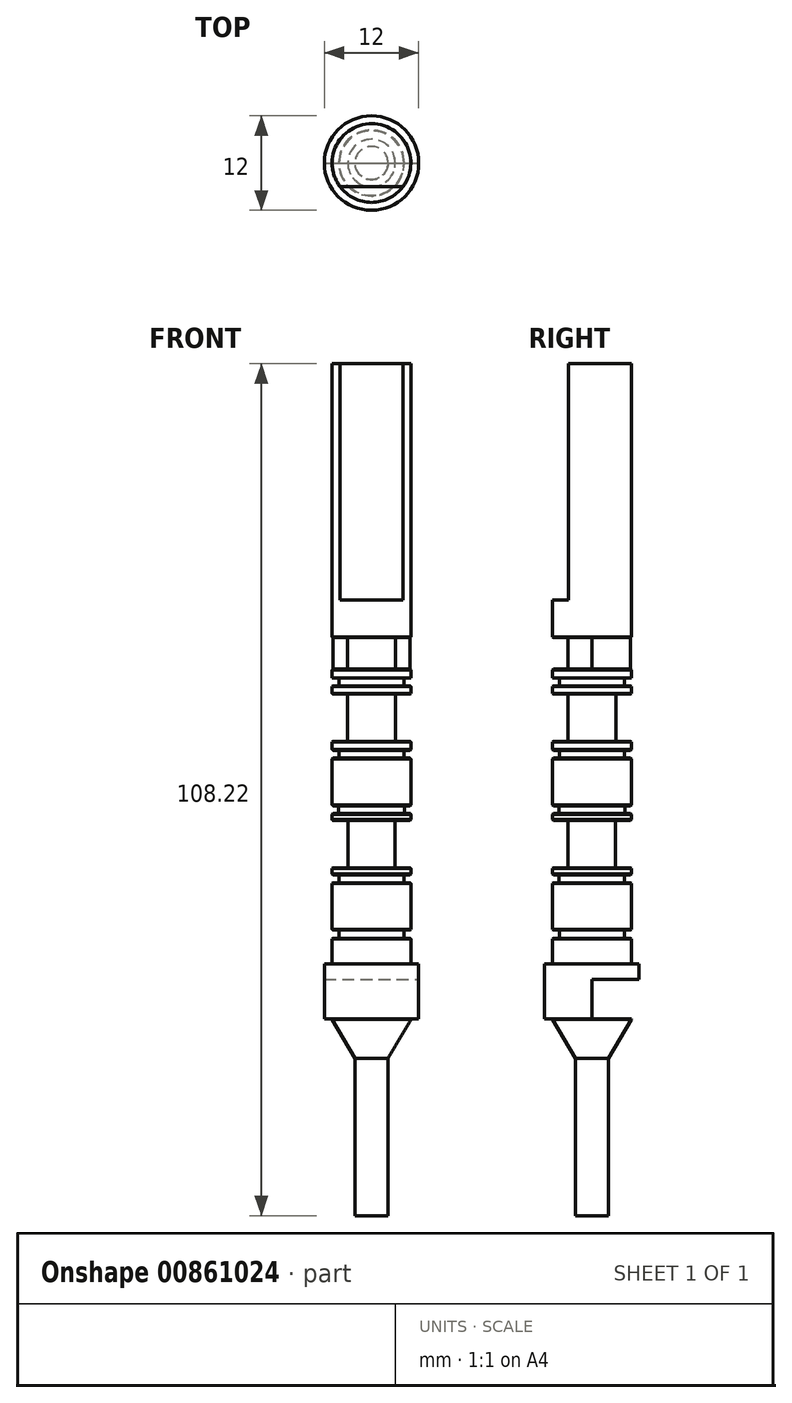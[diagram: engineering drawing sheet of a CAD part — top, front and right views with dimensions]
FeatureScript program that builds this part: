
annotation { "Feature Type Name" : "Feature", "Feature Type Description" : "" }
export const myFeature = defineFeature(function(context is Context, id is Id, definition is map)
    precondition{}
    {
        {
            var Q0;
            Q0=qCreatedBy(makeId("Top.planeOp"),FACE);
            var sketch = newSketch(context, id + "F0", { "sketchPlane" : qUnion([Q0])});
            skCircle(sketch, "E0", {"center": v(0, 0) * mm, "radius": 5 * mm});
            skSolve(sketch);
        }
        {
            var Q0;
            Q0=makeQuery(id+"F0.imprint","IMPRINT",FACE,{"disambiguationData":[TD([[makeQuery(id+"F0.imprint","IMPRINT",EDGE,{"derivedFrom":sQuery(id+"F0.wireOp",EDGE,"E0")}),1.0]])]});
            extrude(context, id + "F1", {"entities" : qUnion([Q0]), "depth" : 25 * mm, "offsetDistance" : 25 * mm});
        }
        {
            var Q0;
            Q0=qCreatedBy(makeId("Right.planeOp"),FACE);
            var sketch = newSketch(context, id + "F2", { "sketchPlane" : qUnion([Q0])});
            skLineSegment(sketch, "E1", {"start": v(0, 18.1) * mm, "end": v(0, 19.09) * mm});
            skLineSegment(sketch, "E2", {"start": v(5.08, 19.09) * mm, "end": v(5.08, 20.08) * mm});
            skLineSegment(sketch, "E3", {"start": v(5.08, 20.08) * mm, "end": v(4.18, 20.08) * mm});
            skLineSegment(sketch, "E4", {"start": v(4.18, 20.08) * mm, "end": v(4.18, 19.09) * mm});
            skLineSegment(sketch, "E5", {"start": v(4.18, 19.09) * mm, "end": v(5.08, 19.09) * mm});
            skSolve(sketch);
        }
        {
            var Q0;
            Q0 = qSketchRegion(id + "F2", true);
            var Q1;
            Q1=sQuery(id+"F2.wireOp",EDGE,"E1");
            revolve(context, id + "F3", {"operationType" : NewBodyOperationType.REMOVE, "surfaceOperationType" : NewSurfaceOperationType.NEW, "entities" : qUnion([Q0]), "axis" : qUnion([Q1]), "revolveType" : RevolveType.FULL, "oppositeDirection" : true});
        }
        {
            var Q0;
            {var subQ0=sQuery(id+"F0.wireOp",EDGE,"E0");var subQ1=makeQuery(id+"F1.opExtrude","CAP_FACE",FACE,{"disambiguationData":[OSD([subQ0])],"isStart":false});Q0=makeQuery(id+"F3.boolean.opBoolean","INTERSECT",EDGE,{"derivedFrom":[makeQuery(id+"FLFBWqMDKXxLfZn_1.boolean.opBoolean","SPLIT",FACE,{"disambiguationData":[TD([subQ1])],"derivedFrom":makeQuery(id+"FGnhcOoFceMI59m_1.boolean.opBoolean","SPLIT",FACE,{"disambiguationData":[TD([subQ1])],"derivedFrom":makeQuery(id+"Fglk9rH2sarWwxm_1.boolean.opBoolean","SPLIT",FACE,{"disambiguationData":[TD([subQ1])],"derivedFrom":makeQuery(id+"F1.opExtrude","SWEPT_FACE",FACE,{"disambiguationData":[OSD([subQ0])]})})})}),makeQuery(id+"F3.opRevolve","SWEPT_FACE",FACE,{"disambiguationData":[OSD([sQuery(id+"F2.wireOp",EDGE,"E5")])]})]});}
            var Q1;
            {var subQ0=sQuery(id+"F0.wireOp",EDGE,"E0");var subQ1=makeQuery(id+"F1.opExtrude","CAP_FACE",FACE,{"disambiguationData":[OSD([subQ0])],"isStart":false});Q1=makeQuery(id+"F3.boolean.opBoolean","INTERSECT",EDGE,{"derivedFrom":[makeQuery(id+"FLFBWqMDKXxLfZn_1.boolean.opBoolean","SPLIT",FACE,{"disambiguationData":[TD([subQ1])],"derivedFrom":makeQuery(id+"FGnhcOoFceMI59m_1.boolean.opBoolean","SPLIT",FACE,{"disambiguationData":[TD([subQ1])],"derivedFrom":makeQuery(id+"Fglk9rH2sarWwxm_1.boolean.opBoolean","SPLIT",FACE,{"disambiguationData":[TD([subQ1])],"derivedFrom":makeQuery(id+"F1.opExtrude","SWEPT_FACE",FACE,{"disambiguationData":[OSD([subQ0])]})})})}),makeQuery(id+"F3.opRevolve","SWEPT_FACE",FACE,{"disambiguationData":[OSD([sQuery(id+"F2.wireOp",EDGE,"E3")])]})]});}
            chamfer(context, id + "F4", {"entities" : qUnion([Q0, Q1]), "width" : 0.1 * mm, "tangentPropagation" : true});
        }
        {
            var Q0;
            Q0=makeQuery(id+"F1.opExtrude","CAP_FACE",FACE,{"disambiguationData":[OSD([sQuery(id+"F0.wireOp",EDGE,"E0")])],"isStart":false});
            var sketch = newSketch(context, id + "F5", { "sketchPlane" : qUnion([Q0])});
            skCircle(sketch, "E6", {"center": v(0, 0) * mm, "radius": 5 * mm});
            skSolve(sketch);
        }
        {
            var Q0;
            Q0=makeQuery(id+"F5.imprint","IMPRINT",FACE,{"disambiguationData":[TD([[makeQuery(id+"F5.imprint","IMPRINT",EDGE,{"derivedFrom":makeQuery(id+"F1.opExtrude","CAP_EDGE",EDGE,{"disambiguationData":[OSD([sQuery(id+"F0.wireOp",EDGE,"E0")])],"isStart":false})}),1.0]])]});
            extrude(context, id + "F6", {"entities" : qUnion([Q0]), "operationType" : NewBodyOperationType.ADD, "depth" : 25 * mm, "offsetDistance" : 25 * mm});
        }
        {
            var Q0;
            Q0=qCreatedBy(makeId("Right.planeOp"),FACE);
            var sketch = newSketch(context, id + "F7", { "sketchPlane" : qUnion([Q0])});
            skLineSegment(sketch, "E7", {"start": v(0, 20.11) * mm, "end": v(0, 26.13) * mm});
            skLineSegment(sketch, "E8", {"start": v(5.03, 26.13) * mm, "end": v(5.03, 27.13) * mm});
            skLineSegment(sketch, "E9", {"start": v(5.03, 27.13) * mm, "end": v(4.1, 27.13) * mm});
            skLineSegment(sketch, "E10", {"start": v(4.1, 27.13) * mm, "end": v(4.1, 26.13) * mm});
            skLineSegment(sketch, "E11", {"start": v(4.1, 26.13) * mm, "end": v(5.03, 26.13) * mm});
            skSolve(sketch);
        }
        {
            var Q0;
            Q0 = qSketchRegion(id + "F7", true);
            var Q1;
            Q1=sQuery(id+"F7.wireOp",EDGE,"E7");
            revolve(context, id + "F8", {"operationType" : NewBodyOperationType.REMOVE, "surfaceOperationType" : NewSurfaceOperationType.NEW, "entities" : qUnion([Q0]), "axis" : qUnion([Q1]), "revolveType" : RevolveType.FULL, "oppositeDirection" : true});
        }
        {
            var Q0;
            Q0=qCreatedBy(makeId("Right.planeOp"),FACE);
            var sketch = newSketch(context, id + "F9", { "sketchPlane" : qUnion([Q0])});
            skLineSegment(sketch, "E12", {"start": v(0, 27.25) * mm, "end": v(0, 28.25) * mm});
            skLineSegment(sketch, "E13", {"start": v(5.03, 28.25) * mm, "end": v(5.03, 34.27) * mm});
            skLineSegment(sketch, "E14", {"start": v(5.03, 34.27) * mm, "end": v(3.02, 34.27) * mm});
            skLineSegment(sketch, "E15", {"start": v(3.02, 34.27) * mm, "end": v(3.02, 28.25) * mm});
            skLineSegment(sketch, "E16", {"start": v(3.02, 28.25) * mm, "end": v(5.03, 28.25) * mm});
            skSolve(sketch);
        }
        {
            var Q0;
            Q0 = qSketchRegion(id + "F9", true);
            var Q1;
            Q1=sQuery(id+"F9.wireOp",EDGE,"E12");
            revolve(context, id + "F10", {"operationType" : NewBodyOperationType.REMOVE, "surfaceOperationType" : NewSurfaceOperationType.NEW, "entities" : qUnion([Q0]), "axis" : qUnion([Q1]), "revolveType" : RevolveType.FULL, "oppositeDirection" : true});
        }
        {
            var Q0;
            {var subQ0=sQuery(id+"F0.wireOp",EDGE,"E0");var subQ1=makeQuery(id+"F1.opExtrude","CAP_FACE",FACE,{"disambiguationData":[OSD([subQ0])],"isStart":false});Q0=makeQuery(id+"F8.boolean.opBoolean","INTERSECT",EDGE,{"derivedFrom":[makeQuery(id+"F6.boolean.opBoolean","MERGE",FACE,{"derivedFrom":[makeQuery(id+"F3.boolean.opBoolean","SPLIT",FACE,{"disambiguationData":[TD([subQ1])],"derivedFrom":makeQuery(id+"FLFBWqMDKXxLfZn_1.boolean.opBoolean","SPLIT",FACE,{"disambiguationData":[TD([subQ1])],"derivedFrom":makeQuery(id+"FGnhcOoFceMI59m_1.boolean.opBoolean","SPLIT",FACE,{"disambiguationData":[TD([subQ1])],"derivedFrom":makeQuery(id+"Fglk9rH2sarWwxm_1.boolean.opBoolean","SPLIT",FACE,{"disambiguationData":[TD([subQ1])],"derivedFrom":makeQuery(id+"F1.opExtrude","SWEPT_FACE",FACE,{"disambiguationData":[OSD([subQ0])]})})})})}),makeQuery(id+"F6.opExtrude","SWEPT_FACE",FACE,{"disambiguationData":[OSD([subQ0])]})]}),makeQuery(id+"F8.opRevolve","SWEPT_FACE",FACE,{"disambiguationData":[OSD([sQuery(id+"F7.wireOp",EDGE,"E11")])]})]});}
            var Q1;
            {var subQ0=sQuery(id+"F0.wireOp",EDGE,"E0");var subQ1=makeQuery(id+"F1.opExtrude","CAP_FACE",FACE,{"disambiguationData":[OSD([subQ0])],"isStart":false});Q1=makeQuery(id+"F8.boolean.opBoolean","INTERSECT",EDGE,{"derivedFrom":[makeQuery(id+"F6.boolean.opBoolean","MERGE",FACE,{"derivedFrom":[makeQuery(id+"F3.boolean.opBoolean","SPLIT",FACE,{"disambiguationData":[TD([subQ1])],"derivedFrom":makeQuery(id+"FLFBWqMDKXxLfZn_1.boolean.opBoolean","SPLIT",FACE,{"disambiguationData":[TD([subQ1])],"derivedFrom":makeQuery(id+"FGnhcOoFceMI59m_1.boolean.opBoolean","SPLIT",FACE,{"disambiguationData":[TD([subQ1])],"derivedFrom":makeQuery(id+"Fglk9rH2sarWwxm_1.boolean.opBoolean","SPLIT",FACE,{"disambiguationData":[TD([subQ1])],"derivedFrom":makeQuery(id+"F1.opExtrude","SWEPT_FACE",FACE,{"disambiguationData":[OSD([subQ0])]})})})})}),makeQuery(id+"F6.opExtrude","SWEPT_FACE",FACE,{"disambiguationData":[OSD([subQ0])]})]}),makeQuery(id+"F8.opRevolve","SWEPT_FACE",FACE,{"disambiguationData":[OSD([sQuery(id+"F7.wireOp",EDGE,"E9")])]})]});}
            var Q2;
            {var subQ0=sQuery(id+"F0.wireOp",EDGE,"E0");var subQ1=makeQuery(id+"F1.opExtrude","CAP_FACE",FACE,{"disambiguationData":[OSD([subQ0])],"isStart":false});Q2=makeQuery(id+"F10.boolean.opBoolean","INTERSECT",EDGE,{"derivedFrom":[makeQuery(id+"F8.boolean.opBoolean","SPLIT",FACE,{"disambiguationData":[TD([makeQuery(id+"F6.opExtrude","CAP_FACE",FACE,{"disambiguationData":[OSD([subQ0])],"isStart":false})])],"derivedFrom":makeQuery(id+"F6.boolean.opBoolean","MERGE",FACE,{"derivedFrom":[makeQuery(id+"F3.boolean.opBoolean","SPLIT",FACE,{"disambiguationData":[TD([subQ1])],"derivedFrom":makeQuery(id+"FLFBWqMDKXxLfZn_1.boolean.opBoolean","SPLIT",FACE,{"disambiguationData":[TD([subQ1])],"derivedFrom":makeQuery(id+"FGnhcOoFceMI59m_1.boolean.opBoolean","SPLIT",FACE,{"disambiguationData":[TD([subQ1])],"derivedFrom":makeQuery(id+"Fglk9rH2sarWwxm_1.boolean.opBoolean","SPLIT",FACE,{"disambiguationData":[TD([subQ1])],"derivedFrom":makeQuery(id+"F1.opExtrude","SWEPT_FACE",FACE,{"disambiguationData":[OSD([subQ0])]})})})})}),makeQuery(id+"F6.opExtrude","SWEPT_FACE",FACE,{"disambiguationData":[OSD([subQ0])]})]})}),makeQuery(id+"F10.opRevolve","SWEPT_FACE",FACE,{"disambiguationData":[OSD([sQuery(id+"F9.wireOp",EDGE,"E16")])]})]});}
            chamfer(context, id + "F11", {"entities" : qUnion([Q0, Q1, Q2]), "width" : 0.1 * mm, "tangentPropagation" : true});
        }
        {
            var Q0;
            Q0=qCreatedBy(makeId("Right.planeOp"),FACE);
            var sketch = newSketch(context, id + "F12", { "sketchPlane" : qUnion([Q0])});
            skLineSegment(sketch, "E17", {"start": v(0, 34.3) * mm, "end": v(0, 35.31) * mm});
            skLineSegment(sketch, "E18", {"start": v(5.03, 35.31) * mm, "end": v(5.03, 36.31) * mm});
            skLineSegment(sketch, "E19", {"start": v(5.03, 36.31) * mm, "end": v(4.1, 36.31) * mm});
            skLineSegment(sketch, "E20", {"start": v(4.1, 36.31) * mm, "end": v(4.1, 35.31) * mm});
            skLineSegment(sketch, "E21", {"start": v(4.1, 35.31) * mm, "end": v(5.03, 35.31) * mm});
            skSolve(sketch);
        }
        {
            var Q0;
            Q0 = qSketchRegion(id + "F12", true);
            var Q1;
            Q1=sQuery(id+"F12.wireOp",EDGE,"E17");
            revolve(context, id + "F13", {"operationType" : NewBodyOperationType.REMOVE, "surfaceOperationType" : NewSurfaceOperationType.NEW, "entities" : qUnion([Q0]), "axis" : qUnion([Q1]), "revolveType" : RevolveType.FULL, "oppositeDirection" : true});
        }
        {
            var Q0;
            {var subQ0=sQuery(id+"F0.wireOp",EDGE,"E0");var subQ1=makeQuery(id+"F1.opExtrude","CAP_FACE",FACE,{"disambiguationData":[OSD([subQ0])],"isStart":false});Q0=makeQuery(id+"F10.boolean.opBoolean","INTERSECT",EDGE,{"derivedFrom":[makeQuery(id+"F8.boolean.opBoolean","SPLIT",FACE,{"disambiguationData":[TD([makeQuery(id+"F6.opExtrude","CAP_FACE",FACE,{"disambiguationData":[OSD([subQ0])],"isStart":false})])],"derivedFrom":makeQuery(id+"F6.boolean.opBoolean","MERGE",FACE,{"derivedFrom":[makeQuery(id+"F3.boolean.opBoolean","SPLIT",FACE,{"disambiguationData":[TD([subQ1])],"derivedFrom":makeQuery(id+"FLFBWqMDKXxLfZn_1.boolean.opBoolean","SPLIT",FACE,{"disambiguationData":[TD([subQ1])],"derivedFrom":makeQuery(id+"FGnhcOoFceMI59m_1.boolean.opBoolean","SPLIT",FACE,{"disambiguationData":[TD([subQ1])],"derivedFrom":makeQuery(id+"Fglk9rH2sarWwxm_1.boolean.opBoolean","SPLIT",FACE,{"disambiguationData":[TD([subQ1])],"derivedFrom":makeQuery(id+"F1.opExtrude","SWEPT_FACE",FACE,{"disambiguationData":[OSD([subQ0])]})})})})}),makeQuery(id+"F6.opExtrude","SWEPT_FACE",FACE,{"disambiguationData":[OSD([subQ0])]})]})}),makeQuery(id+"F10.opRevolve","SWEPT_FACE",FACE,{"disambiguationData":[OSD([sQuery(id+"F9.wireOp",EDGE,"E14")])]})]});}
            var Q1;
            {var subQ0=sQuery(id+"F0.wireOp",EDGE,"E0");var subQ1=makeQuery(id+"F6.opExtrude","CAP_FACE",FACE,{"disambiguationData":[OSD([subQ0])],"isStart":false});var subQ2=makeQuery(id+"F1.opExtrude","CAP_FACE",FACE,{"disambiguationData":[OSD([subQ0])],"isStart":false});Q1=makeQuery(id+"F13.boolean.opBoolean","INTERSECT",EDGE,{"derivedFrom":[makeQuery(id+"F10.boolean.opBoolean","SPLIT",FACE,{"disambiguationData":[TD([subQ1])],"derivedFrom":makeQuery(id+"F8.boolean.opBoolean","SPLIT",FACE,{"disambiguationData":[TD([subQ1])],"derivedFrom":makeQuery(id+"F6.boolean.opBoolean","MERGE",FACE,{"derivedFrom":[makeQuery(id+"F3.boolean.opBoolean","SPLIT",FACE,{"disambiguationData":[TD([subQ2])],"derivedFrom":makeQuery(id+"FLFBWqMDKXxLfZn_1.boolean.opBoolean","SPLIT",FACE,{"disambiguationData":[TD([subQ2])],"derivedFrom":makeQuery(id+"FGnhcOoFceMI59m_1.boolean.opBoolean","SPLIT",FACE,{"disambiguationData":[TD([subQ2])],"derivedFrom":makeQuery(id+"Fglk9rH2sarWwxm_1.boolean.opBoolean","SPLIT",FACE,{"disambiguationData":[TD([subQ2])],"derivedFrom":makeQuery(id+"F1.opExtrude","SWEPT_FACE",FACE,{"disambiguationData":[OSD([subQ0])]})})})})}),makeQuery(id+"F6.opExtrude","SWEPT_FACE",FACE,{"disambiguationData":[OSD([subQ0])]})]})})}),makeQuery(id+"F13.opRevolve","SWEPT_FACE",FACE,{"disambiguationData":[OSD([sQuery(id+"F12.wireOp",EDGE,"E21")])]})]});}
            chamfer(context, id + "F14", {"entities" : qUnion([Q0, Q1]), "width" : 0.1 * mm, "tangentPropagation" : true});
        }
        {
            var Q0;
            Q0=qCreatedBy(makeId("Right.planeOp"),FACE);
            var sketch = newSketch(context, id + "F15", { "sketchPlane" : qUnion([Q0])});
            skLineSegment(sketch, "E22", {"start": v(0, 19.22) * mm, "end": v(0, 18.21) * mm});
            skLineSegment(sketch, "E23", {"start": v(-5.02, 18.21) * mm, "end": v(-5.02, 12.2) * mm});
            skLineSegment(sketch, "E24", {"start": v(-5.02, 12.2) * mm, "end": v(-3.01, 12.2) * mm});
            skLineSegment(sketch, "E25", {"start": v(-3.01, 12.2) * mm, "end": v(-3.01, 18.21) * mm});
            skLineSegment(sketch, "E26", {"start": v(-3.01, 18.21) * mm, "end": v(-5.02, 18.21) * mm});
            skSolve(sketch);
        }
        {
            var Q0;
            Q0 = qSketchRegion(id + "F15", true);
            var Q1;
            Q1=sQuery(id+"F15.wireOp",EDGE,"E22");
            revolve(context, id + "F16", {"operationType" : NewBodyOperationType.REMOVE, "surfaceOperationType" : NewSurfaceOperationType.NEW, "entities" : qUnion([Q0]), "axis" : qUnion([Q1]), "revolveType" : RevolveType.FULL, "oppositeDirection" : true});
        }
        {
            var Q0;
            Q0=qCreatedBy(makeId("Right.planeOp"),FACE);
            var sketch = newSketch(context, id + "F17", { "sketchPlane" : qUnion([Q0])});
            skLineSegment(sketch, "E27", {"start": v(0, 12.3) * mm, "end": v(0, 11.3) * mm});
            skLineSegment(sketch, "E28", {"start": v(-5.06, 11.3) * mm, "end": v(-5.06, 10.3) * mm});
            skLineSegment(sketch, "E29", {"start": v(-5.06, 10.3) * mm, "end": v(-4.16, 10.3) * mm});
            skLineSegment(sketch, "E30", {"start": v(-4.16, 10.3) * mm, "end": v(-4.16, 11.3) * mm});
            skLineSegment(sketch, "E31", {"start": v(-4.16, 11.3) * mm, "end": v(-5.06, 11.3) * mm});
            skSolve(sketch);
        }
        {
            var Q0;
            Q0 = qSketchRegion(id + "F17", true);
            var Q1;
            Q1=sQuery(id+"F17.wireOp",EDGE,"E27");
            revolve(context, id + "F18", {"operationType" : NewBodyOperationType.REMOVE, "surfaceOperationType" : NewSurfaceOperationType.NEW, "entities" : qUnion([Q0]), "axis" : qUnion([Q1]), "revolveType" : RevolveType.FULL, "oppositeDirection" : true});
        }
        {
            var Q0;
            Q0=qCreatedBy(makeId("Right.planeOp"),FACE);
            var sketch = newSketch(context, id + "F19", { "sketchPlane" : qUnion([Q0])});
            skLineSegment(sketch, "E32", {"start": v(0, 10.27) * mm, "end": v(0, 4.27) * mm});
            skLineSegment(sketch, "E33", {"start": v(-5.01, 4.27) * mm, "end": v(-5.01, 3.25) * mm});
            skLineSegment(sketch, "E34", {"start": v(-5.01, 3.25) * mm, "end": v(-4.1, 3.25) * mm});
            skLineSegment(sketch, "E35", {"start": v(-4.1, 3.25) * mm, "end": v(-4.1, 4.27) * mm});
            skLineSegment(sketch, "E36", {"start": v(-4.1, 4.27) * mm, "end": v(-5.01, 4.27) * mm});
            skSolve(sketch);
        }
        {
            var Q0;
            Q0 = qSketchRegion(id + "F19", true);
            var Q1;
            Q1=sQuery(id+"F19.wireOp",EDGE,"E32");
            revolve(context, id + "F20", {"operationType" : NewBodyOperationType.REMOVE, "surfaceOperationType" : NewSurfaceOperationType.NEW, "entities" : qUnion([Q0]), "axis" : qUnion([Q1]), "revolveType" : RevolveType.FULL, "oppositeDirection" : true});
        }
        {
            var Q0;
            {var subQ0=sQuery(id+"F0.wireOp",EDGE,"E0");var subQ1=makeQuery(id+"F1.opExtrude","CAP_FACE",FACE,{"disambiguationData":[OSD([subQ0])],"isStart":true});Q0=makeQuery(id+"F20.boolean.opBoolean","INTERSECT",EDGE,{"derivedFrom":[makeQuery(id+"F18.boolean.opBoolean","SPLIT",FACE,{"disambiguationData":[TD([subQ1])],"derivedFrom":makeQuery(id+"F16.boolean.opBoolean","SPLIT",FACE,{"disambiguationData":[TD([subQ1])],"derivedFrom":makeQuery(id+"F3.boolean.opBoolean","SPLIT",FACE,{"disambiguationData":[TD([subQ1])],"derivedFrom":makeQuery(id+"F1.opExtrude","SWEPT_FACE",FACE,{"disambiguationData":[OSD([subQ0])]})})})}),makeQuery(id+"F20.opRevolve","SWEPT_FACE",FACE,{"disambiguationData":[OSD([sQuery(id+"F19.wireOp",EDGE,"E34")])]})]});}
            var Q1;
            {var subQ0=sQuery(id+"F0.wireOp",EDGE,"E0");var subQ1=makeQuery(id+"F1.opExtrude","CAP_FACE",FACE,{"disambiguationData":[OSD([subQ0])],"isStart":true});Q1=makeQuery(id+"F20.boolean.opBoolean","INTERSECT",EDGE,{"derivedFrom":[makeQuery(id+"F18.boolean.opBoolean","SPLIT",FACE,{"disambiguationData":[TD([subQ1])],"derivedFrom":makeQuery(id+"F16.boolean.opBoolean","SPLIT",FACE,{"disambiguationData":[TD([subQ1])],"derivedFrom":makeQuery(id+"F3.boolean.opBoolean","SPLIT",FACE,{"disambiguationData":[TD([subQ1])],"derivedFrom":makeQuery(id+"F1.opExtrude","SWEPT_FACE",FACE,{"disambiguationData":[OSD([subQ0])]})})})}),makeQuery(id+"F20.opRevolve","SWEPT_FACE",FACE,{"disambiguationData":[OSD([sQuery(id+"F19.wireOp",EDGE,"E36")])]})]});}
            var Q2;
            {var subQ0=sQuery(id+"F0.wireOp",EDGE,"E0");var subQ1=makeQuery(id+"F1.opExtrude","CAP_FACE",FACE,{"disambiguationData":[OSD([subQ0])],"isStart":true});Q2=makeQuery(id+"F18.boolean.opBoolean","INTERSECT",EDGE,{"derivedFrom":[makeQuery(id+"F16.boolean.opBoolean","SPLIT",FACE,{"disambiguationData":[TD([subQ1])],"derivedFrom":makeQuery(id+"F3.boolean.opBoolean","SPLIT",FACE,{"disambiguationData":[TD([subQ1])],"derivedFrom":makeQuery(id+"F1.opExtrude","SWEPT_FACE",FACE,{"disambiguationData":[OSD([subQ0])]})})}),makeQuery(id+"F18.opRevolve","SWEPT_FACE",FACE,{"disambiguationData":[OSD([sQuery(id+"F17.wireOp",EDGE,"E29")])]})]});}
            var Q3;
            {var subQ0=sQuery(id+"F0.wireOp",EDGE,"E0");var subQ1=makeQuery(id+"F1.opExtrude","CAP_FACE",FACE,{"disambiguationData":[OSD([subQ0])],"isStart":true});Q3=makeQuery(id+"F18.boolean.opBoolean","INTERSECT",EDGE,{"derivedFrom":[makeQuery(id+"F16.boolean.opBoolean","SPLIT",FACE,{"disambiguationData":[TD([subQ1])],"derivedFrom":makeQuery(id+"F3.boolean.opBoolean","SPLIT",FACE,{"disambiguationData":[TD([subQ1])],"derivedFrom":makeQuery(id+"F1.opExtrude","SWEPT_FACE",FACE,{"disambiguationData":[OSD([subQ0])]})})}),makeQuery(id+"F18.opRevolve","SWEPT_FACE",FACE,{"disambiguationData":[OSD([sQuery(id+"F17.wireOp",EDGE,"E31")])]})]});}
            var Q4;
            {var subQ0=sQuery(id+"F0.wireOp",EDGE,"E0");Q4=makeQuery(id+"F16.boolean.opBoolean","INTERSECT",EDGE,{"derivedFrom":[makeQuery(id+"F3.boolean.opBoolean","SPLIT",FACE,{"disambiguationData":[TD([makeQuery(id+"F1.opExtrude","CAP_FACE",FACE,{"disambiguationData":[OSD([subQ0])],"isStart":true})])],"derivedFrom":makeQuery(id+"F1.opExtrude","SWEPT_FACE",FACE,{"disambiguationData":[OSD([subQ0])]})}),makeQuery(id+"F16.opRevolve","SWEPT_FACE",FACE,{"disambiguationData":[OSD([sQuery(id+"F15.wireOp",EDGE,"E24")])]})]});}
            var Q5;
            {var subQ0=sQuery(id+"F0.wireOp",EDGE,"E0");Q5=makeQuery(id+"F16.boolean.opBoolean","INTERSECT",EDGE,{"derivedFrom":[makeQuery(id+"F3.boolean.opBoolean","SPLIT",FACE,{"disambiguationData":[TD([makeQuery(id+"F1.opExtrude","CAP_FACE",FACE,{"disambiguationData":[OSD([subQ0])],"isStart":true})])],"derivedFrom":makeQuery(id+"F1.opExtrude","SWEPT_FACE",FACE,{"disambiguationData":[OSD([subQ0])]})}),makeQuery(id+"F16.opRevolve","SWEPT_FACE",FACE,{"disambiguationData":[OSD([sQuery(id+"F15.wireOp",EDGE,"E26")])]})]});}
            chamfer(context, id + "F21", {"entities" : qUnion([Q0, Q1, Q2, Q3, Q4, Q5]), "width" : 0.1 * mm, "tangentPropagation" : true});
        }
        {
            var Q0;
            Q0=makeQuery(id+"F1.opExtrude","CAP_FACE",FACE,{"disambiguationData":[OSD([sQuery(id+"F0.wireOp",EDGE,"E0")])],"isStart":true});
            var sketch = newSketch(context, id + "F22", { "sketchPlane" : qUnion([Q0])});
            skCircle(sketch, "E37", {"center": v(0, 0) * mm, "radius": 6 * mm});
            skSolve(sketch);
        }
        {
            var Q0;
            Q0 = qSketchRegion(id + "F22", true);
            extrude(context, id + "F23", {"entities" : qUnion([Q0]), "operationType" : NewBodyOperationType.ADD, "depth" : 7 * mm, "offsetDistance" : 25 * mm});
        }
        {
            var Q0;
            Q0=makeQuery(id+"F23.opExtrude","CAP_FACE",FACE,{"disambiguationData":[OSD([sQuery(id+"F22.wireOp",EDGE,"E37")])],"isStart":false});
            var sketch = newSketch(context, id + "F24", { "sketchPlane" : qUnion([Q0])});
            skLineSegment(sketch, "E38.bottom", {"start": v(-6, 0) * mm, "end": v(6.03, 0) * mm});
            skLineSegment(sketch, "E38.top", {"start": v(-6, -6.15) * mm, "end": v(6.03, -6.15) * mm});
            skLineSegment(sketch, "E38.left", {"start": v(-6, 0) * mm, "end": v(-6, -6.15) * mm});
            skLineSegment(sketch, "E38.right", {"start": v(6.03, 0) * mm, "end": v(6.03, -6.15) * mm});
            skSolve(sketch);
        }
        {
            var Q0;
            Q0 = qSketchRegion(id + "F24", true);
            extrude(context, id + "F25", {"entities" : qUnion([Q0]), "operationType" : NewBodyOperationType.REMOVE, "oppositeDirection" : true, "depth" : 5 * mm, "offsetDistance" : 25 * mm});
        }
        {
            var Q0;
            Q0=makeQuery(id+"F23.opExtrude","CAP_FACE",FACE,{"disambiguationData":[OSD([sQuery(id+"F22.wireOp",EDGE,"E37")])],"isStart":false});
            var sketch = newSketch(context, id + "F26", { "sketchPlane" : qUnion([Q0])});
            skCircle(sketch, "E39", {"center": v(0, 0) * mm, "radius": 5 * mm});
            skSolve(sketch);
        }
        {
            var Q0;
            Q0 = qSketchRegion(id + "F26", true);
            extrude(context, id + "F27", {"entities" : qUnion([Q0]), "operationType" : NewBodyOperationType.ADD, "depth" : 5 * mm, "offsetDistance" : 25 * mm});
        }
        {
            var Q0;
            Q0=qCreatedBy(makeId("Right.planeOp"),FACE);
            var sketch = newSketch(context, id + "F28", { "sketchPlane" : qUnion([Q0])});
            skLineSegment(sketch, "E40", {"start": v(0, -7.05) * mm, "end": v(0, -12.15) * mm});
            skLineSegment(sketch, "E41", {"start": v(-5.03, -12.15) * mm, "end": v(-5.03, -7.05) * mm});
            skLineSegment(sketch, "E42", {"start": v(-2, -12.15) * mm, "end": v(-5.03, -12.15) * mm});
            skLineSegment(sketch, "E43", {"start": v(-2, -12.15) * mm, "end": v(-5.03, -7.05) * mm});
            skSolve(sketch);
        }
        {
            var Q0;
            Q0 = qSketchRegion(id + "F28", true);
            var Q1;
            Q1=sQuery(id+"F28.wireOp",EDGE,"E40");
            revolve(context, id + "F29", {"operationType" : NewBodyOperationType.REMOVE, "surfaceOperationType" : NewSurfaceOperationType.NEW, "entities" : qUnion([Q0]), "axis" : qUnion([Q1]), "revolveType" : RevolveType.FULL, "oppositeDirection" : true});
        }
        {
            var Q0;
            Q0=makeQuery(id+"F27.opExtrude","CAP_FACE",FACE,{"disambiguationData":[OSD([sQuery(id+"F26.wireOp",EDGE,"E39")])],"isStart":false});
            var sketch = newSketch(context, id + "F30", { "sketchPlane" : qUnion([Q0])});
            skCircle(sketch, "E44", {"center": v(0, 0) * mm, "radius": 2.1 * mm});
            skSolve(sketch);
        }
        {
            var Q0;
            Q0 = qSketchRegion(id + "F30", true);
            extrude(context, id + "F31", {"entities" : qUnion([Q0]), "operationType" : NewBodyOperationType.ADD, "depth" : 20 * mm, "offsetDistance" : 25 * mm});
        }
        {
            var Q0;
            Q0=qCreatedBy(makeId("Right.planeOp"),FACE);
            var sketch = newSketch(context, id + "F32", { "sketchPlane" : qUnion([Q0])});
            skLineSegment(sketch, "E45", {"start": v(0, 36.4) * mm, "end": v(0, 37.43) * mm});
            skLineSegment(sketch, "E46", {"start": v(-5.02, 37.43) * mm, "end": v(-5.02, 41.42) * mm});
            skLineSegment(sketch, "E47", {"start": v(-5.02, 41.42) * mm, "end": v(-3.02, 41.42) * mm});
            skLineSegment(sketch, "E48", {"start": v(-3.02, 41.42) * mm, "end": v(-3.02, 37.43) * mm});
            skLineSegment(sketch, "E49", {"start": v(-3.02, 37.43) * mm, "end": v(-5.02, 37.43) * mm});
            skSolve(sketch);
        }
        {
            var Q0;
            Q0 = qSketchRegion(id + "F32", true);
            var Q1;
            Q1=sQuery(id+"F32.wireOp",EDGE,"E45");
            revolve(context, id + "F33", {"operationType" : NewBodyOperationType.REMOVE, "surfaceOperationType" : NewSurfaceOperationType.NEW, "entities" : qUnion([Q0]), "axis" : qUnion([Q1]), "revolveType" : RevolveType.FULL, "oppositeDirection" : true});
        }
        {
            var Q0;
            {var subQ0=sQuery(id+"F0.wireOp",EDGE,"E0");var subQ1=makeQuery(id+"F6.opExtrude","CAP_FACE",FACE,{"disambiguationData":[OSD([subQ0])],"isStart":false});Q0=makeQuery(id+"F33.boolean.opBoolean","INTERSECT",EDGE,{"derivedFrom":[makeQuery(id+"F13.boolean.opBoolean","SPLIT",FACE,{"disambiguationData":[TD([subQ1])],"derivedFrom":makeQuery(id+"F10.boolean.opBoolean","SPLIT",FACE,{"disambiguationData":[TD([subQ1])],"derivedFrom":makeQuery(id+"F8.boolean.opBoolean","SPLIT",FACE,{"disambiguationData":[TD([subQ1])],"derivedFrom":makeQuery(id+"F6.boolean.opBoolean","MERGE",FACE,{"derivedFrom":[makeQuery(id+"F3.boolean.opBoolean","SPLIT",FACE,{"disambiguationData":[TD([makeQuery(id+"F1.opExtrude","CAP_FACE",FACE,{"disambiguationData":[OSD([subQ0])],"isStart":false})])],"derivedFrom":makeQuery(id+"F1.opExtrude","SWEPT_FACE",FACE,{"disambiguationData":[OSD([subQ0])]})}),makeQuery(id+"F6.opExtrude","SWEPT_FACE",FACE,{"disambiguationData":[OSD([subQ0])]})]})})})}),makeQuery(id+"F33.opRevolve","SWEPT_FACE",FACE,{"disambiguationData":[OSD([sQuery(id+"F32.wireOp",EDGE,"E49")])]})]});}
            var Q1;
            {var subQ0=sQuery(id+"F0.wireOp",EDGE,"E0");var subQ1=makeQuery(id+"F6.opExtrude","CAP_FACE",FACE,{"disambiguationData":[OSD([subQ0])],"isStart":false});Q1=makeQuery(id+"F33.boolean.opBoolean","INTERSECT",EDGE,{"derivedFrom":[makeQuery(id+"F13.boolean.opBoolean","SPLIT",FACE,{"disambiguationData":[TD([subQ1])],"derivedFrom":makeQuery(id+"F10.boolean.opBoolean","SPLIT",FACE,{"disambiguationData":[TD([subQ1])],"derivedFrom":makeQuery(id+"F8.boolean.opBoolean","SPLIT",FACE,{"disambiguationData":[TD([subQ1])],"derivedFrom":makeQuery(id+"F6.boolean.opBoolean","MERGE",FACE,{"derivedFrom":[makeQuery(id+"F3.boolean.opBoolean","SPLIT",FACE,{"disambiguationData":[TD([makeQuery(id+"F1.opExtrude","CAP_FACE",FACE,{"disambiguationData":[OSD([subQ0])],"isStart":false})])],"derivedFrom":makeQuery(id+"F1.opExtrude","SWEPT_FACE",FACE,{"disambiguationData":[OSD([subQ0])]})}),makeQuery(id+"F6.opExtrude","SWEPT_FACE",FACE,{"disambiguationData":[OSD([subQ0])]})]})})})}),makeQuery(id+"F33.opRevolve","SWEPT_FACE",FACE,{"disambiguationData":[OSD([sQuery(id+"F32.wireOp",EDGE,"E47")])]})]});}
            chamfer(context, id + "F34", {"entities" : qUnion([Q0, Q1]), "width" : 0.1 * mm, "tangentPropagation" : true});
        }
        {
            var Q0;
            Q0=makeQuery(id+"F6.opExtrude","CAP_FACE",FACE,{"disambiguationData":[OSD([sQuery(id+"F0.wireOp",EDGE,"E0")])],"isStart":false});
            var sketch = newSketch(context, id + "F35", { "sketchPlane" : qUnion([Q0])});
            skCircle(sketch, "E50", {"center": v(0, 0) * mm, "radius": 5 * mm});
            skSolve(sketch);
        }
        {
            var Q0;
            Q0=makeQuery(id+"F35.imprint","IMPRINT",FACE,{"disambiguationData":[TD([[makeQuery(id+"F35.imprint","IMPRINT",EDGE,{"derivedFrom":sQuery(id+"F35.wireOp",EDGE,"E50")}),1.0]])]});
            extrude(context, id + "F36", {"entities" : qUnion([Q0]), "operationType" : NewBodyOperationType.ADD, "depth" : 26.22 * mm, "offsetDistance" : 25 * mm});
        }
        {
            var Q0;
            Q0=makeQuery(id+"F36.opExtrude","CAP_FACE",FACE,{"disambiguationData":[OSD([sQuery(id+"F35.wireOp",EDGE,"E50")])],"isStart":false});
            var sketch = newSketch(context, id + "F37", { "sketchPlane" : qUnion([Q0])});
            skLineSegment(sketch, "E51", {"start": v(0, -5) * mm, "end": v(5, -5) * mm});
            skLineSegment(sketch, "E52", {"start": v(5, -5) * mm, "end": v(5, -3) * mm});
            skLineSegment(sketch, "E53", {"start": v(5, -3) * mm, "end": v(-5, -3) * mm});
            skLineSegment(sketch, "E54", {"start": v(-5, -3) * mm, "end": v(-5, -5) * mm});
            skLineSegment(sketch, "E55", {"start": v(-5, -5) * mm, "end": v(0, -5) * mm});
            skSolve(sketch);
        }
        {
            var Q0;
            {var subQ0=sQuery(id+"F37.wireOp",EDGE,"E53");var subQ1=makeQuery(id+"F36.opExtrude","CAP_EDGE",EDGE,{"disambiguationData":[OSD([sQuery(id+"F35.wireOp",EDGE,"E50")])],"isStart":false});var subQ2=makeQuery(id+"F37.imprint","INTERSECT",VERTEX,{"disambiguationData":[OD(0.0)],"derivedFrom":[subQ1,subQ0]});Q0=makeQuery(id+"F37.imprint","IMPRINT",FACE,{"disambiguationData":[TD([[makeQuery(id+"F37.imprint","IMPRINT",EDGE,{"disambiguationData":[TD([[subQ2,-1.0]])],"derivedFrom":subQ0}),1.0]])]});}
            extrude(context, id + "F38", {"entities" : qUnion([Q0]), "operationType" : NewBodyOperationType.REMOVE, "oppositeDirection" : true, "depth" : 30 * mm, "offsetDistance" : 25 * mm});
        }
        {
            var Q0;
            Q0=makeQuery(id+"F33.boolean.opBoolean","COPY",FACE,{"derivedFrom":makeQuery(id+"F33.opRevolve","SWEPT_FACE",FACE,{"disambiguationData":[OSD([sQuery(id+"F32.wireOp",EDGE,"E47")])]})});
            var sketch = newSketch(context, id + "F39", { "sketchPlane" : qUnion([Q0])});
            skArc(sketch, "E56", {"start": v(4.9, 0) * mm, "mid": v(0, -4.9) * mm, "end": v(-4.9, 0) * mm});
            skLineSegment(sketch, "E57", {"start": v(-4.9, 0) * mm, "end": v(4.9, 0) * mm});
            skSolve(sketch);
        }
        {
            var Q0;
            Q0 = qSketchRegion(id + "F39", true);
            extrude(context, id + "F40", {"entities" : qUnion([Q0]), "operationType" : NewBodyOperationType.ADD, "depth" : 5 * mm, "offsetDistance" : 25 * mm});
        }
    });
